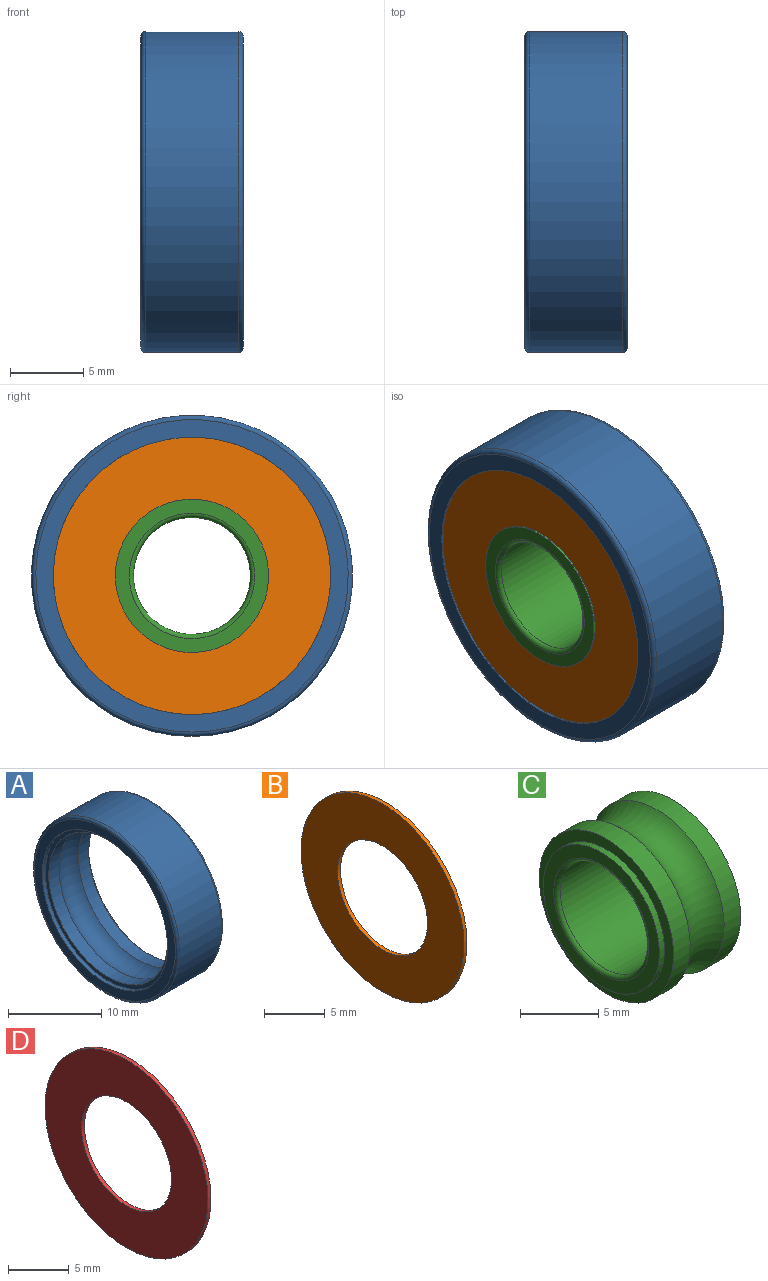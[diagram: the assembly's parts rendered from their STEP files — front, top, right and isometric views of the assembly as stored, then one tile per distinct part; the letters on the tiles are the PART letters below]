
ASSEMBLY  parts=4 mates=6
PART A: 12 faces, bbox 7x23.8x23.8 mm
  f0: plane 21.4x21.4mm, normal (-1,0,0), area 76.2mm2, adj f1,f11
  f1: cylinder r=9.5mm len=19mm, axis (1,0,0), area 27.7mm2, adj f0,f2
  f2: plane 19x19mm, normal (-1,0,0), area 29.6mm2, adj f1,f3
  f3: cylinder r=8.99mm len=17.98mm, axis (1,0,0), area 87.9mm2, adj f2,f4
  f4: torus R=7.5mm, axis (1,0,0), area 193.8mm2, adj f3,f5
  f5: cylinder r=8.99mm len=17.98mm, axis (1,0,0), area 87.9mm2, adj f4,f6
  f6: plane 19x19mm, normal (1,0,0), area 29.6mm2, adj f5,f7
  f7: cylinder r=9.5mm len=19mm, axis (1,0,0), area 27.7mm2, adj f6,f8
  f8: plane 21.4x21.4mm, normal (1,0,0), area 76.2mm2, adj f7,f9
  f9: torus R=10.7mm, axis (1,0,0), area 32.2mm2, adj f8,f10
  f10: cylinder r=11mm len=22mm, axis (1,0,0), area 442.3mm2, adj f9,f11
  f11: torus R=10.7mm, axis (1,0,0), area 32.2mm2, adj f0,f10
PART B: 4 faces, bbox 0.3x19x19 mm
  f0: plane 19x19mm, normal (-1,0,0), area 196.9mm2, adj f1,f3
  f1: cylinder r=5.25mm len=10.5mm, axis (1,0,0), area 11.5mm2, adj f0,f2
  f2: plane 19x19mm, normal (1,0,0), area 196.9mm2, adj f1,f3
  f3: cylinder r=9.5mm len=19mm, axis (1,0,0), area 20.8mm2, adj f0,f2
PART C: 12 faces, bbox 7x16.2x16.2 mm
  f0: plane 10.5x10.5mm, normal (-1,0,0), area 28.5mm2, adj f1,f11
  f1: torus R=4.3mm, axis (1,0,0), area 12.2mm2, adj f0,f2
  f2: cylinder r=4mm len=8mm, axis (1,0,0), area 160.8mm2, adj f1,f3
  f3: torus R=4.3mm, axis (1,0,0), area 12.2mm2, adj f2,f4
  f4: plane 10.5x10.5mm, normal (1,0,0), area 28.5mm2, adj f3,f5
  f5: cylinder r=5.25mm len=10.5mm, axis (1,0,0), area 15.3mm2, adj f4,f6
  f6: plane 12.14x12.14mm, normal (1,0,0), area 29.2mm2, adj f5,f7
  f7: cylinder r=6.07mm len=12.14mm, axis (1,0,0), area 57.1mm2, adj f6,f8
  f8: torus R=7.5mm, axis (1,0,0), area 122.1mm2, adj f7,f9
  f9: cylinder r=6.07mm len=12.14mm, axis (1,0,0), area 57.1mm2, adj f8,f10
  f10: plane 12.14x12.14mm, normal (-1,0,0), area 29.2mm2, adj f9,f11
  f11: cylinder r=5.25mm len=10.5mm, axis (1,0,0), area 15.3mm2, adj f0,f10
PART D: 4 faces, bbox 0.3x19x19 mm
  f0: plane 19x19mm, normal (-1,0,0), area 196.9mm2, adj f1,f3
  f1: cylinder r=5.25mm len=10.5mm, axis (1,0,0), area 11.5mm2, adj f0,f2
  f2: plane 19x19mm, normal (1,0,0), area 196.9mm2, adj f1,f3
  f3: cylinder r=9.5mm len=19mm, axis (1,0,0), area 20.8mm2, adj f0,f2
PLACE A t=(-23.75,-13.34,11.5)mm
PLACE B rot(axis=(0,-0.71,0.71),180deg) t=(-22.82,-13.34,11.5)mm
PLACE C rot(axis=(1,0,0),90deg) t=(-23.75,-13.34,11.5)mm
PLACE D rot(axis=(1,0,0),0deg) t=(-23.75,-13.34,11.5)mm
MATE cylindrical D.f1 <-> C.f1  axis (1,0,0) through (-17.04,-13.34,11.5)mm
MATE planar C.f1 <-> B.f1  axis (-1,0,0) through (-23.28,-13.34,11.5)mm
MATE planar A.f1 <-> C.f1  axis (-1,0,0) through (-23.75,-13.34,11.5)mm
MATE planar D.f1 <-> A.f1  axis (-1,0,0) through (-17.21,-13.34,11.5)mm
MATE cylindrical A.f1 <-> C.f1  axis (1,0,0) through (-22.5,-13.34,11.5)mm
MATE cylindrical B.f1 <-> C.f1  axis (-1,0,0) through (-23.46,-13.34,11.5)mm
